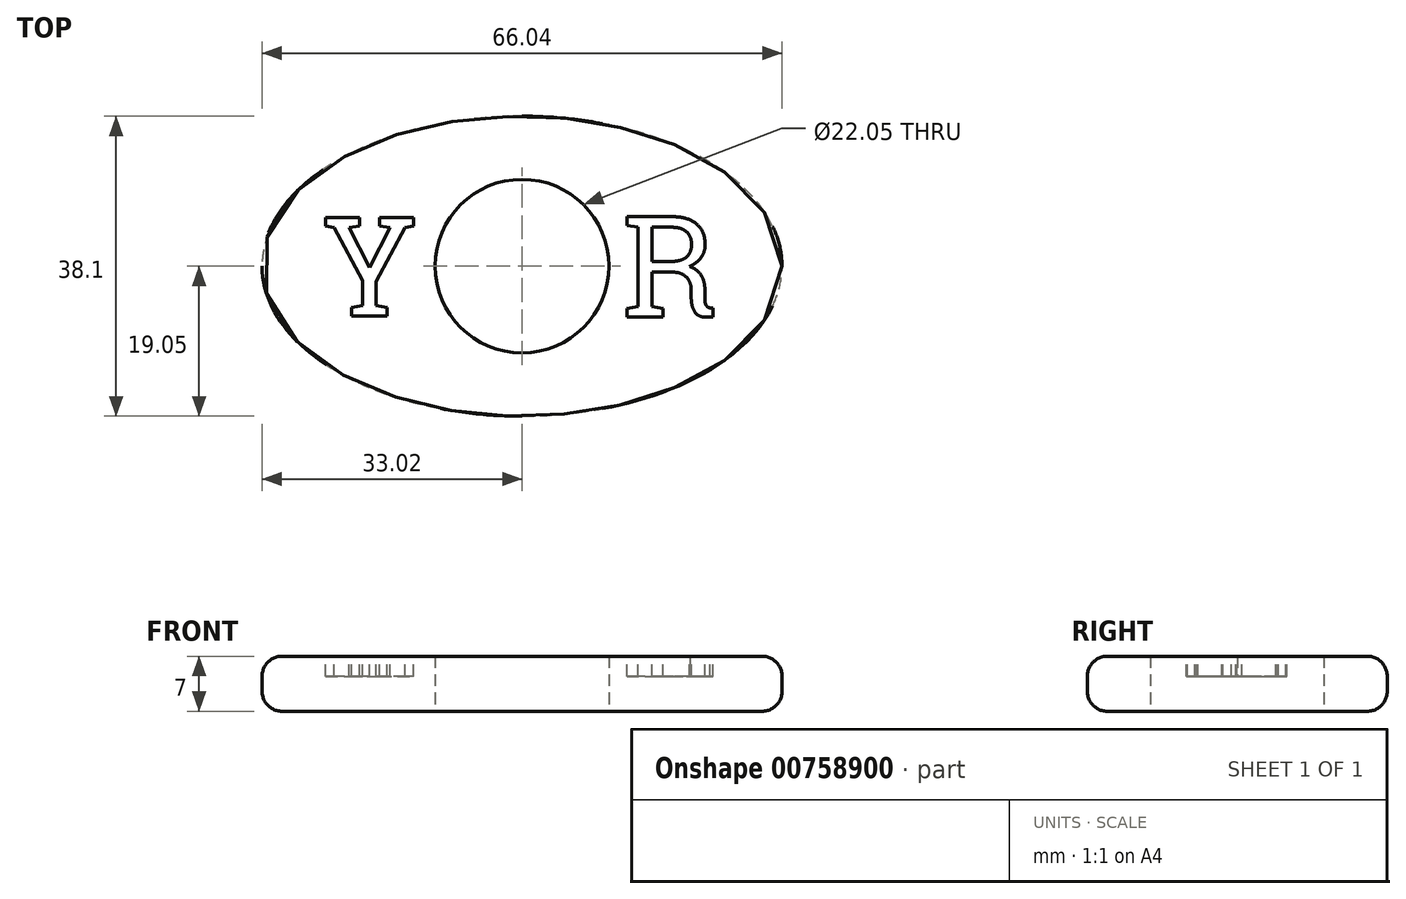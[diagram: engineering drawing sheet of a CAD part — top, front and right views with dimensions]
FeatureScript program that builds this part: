
annotation { "Feature Type Name" : "Feature", "Feature Type Description" : "" }
export const myFeature = defineFeature(function(context is Context, id is Id, definition is map)
    precondition{}
    {
        {
            var Q0;
            Q0=qCreatedBy(makeId("Top.planeOp"),FACE);
            var sketch = newSketch(context, id + "F0", { "sketchPlane" : qUnion([Q0])});
            skEllipse(sketch, "E0", {"center": v(0, 0) * mm, "majorRadius": 33.02 * mm, "minorRadius": 19.05 * mm, "majorAxis": v(1, 0)});
            skCircle(sketch, "E1", {"center": v(0, 0) * mm, "radius": 11.03 * mm});
            skLineSegment(sketch, "E2", {"start": v(-33.02, 0) * mm, "end": v(33.02, 0) * mm, "construction": true});
            skLineSegment(sketch, "E3", {"start": v(0, 19.05) * mm, "end": v(0, -19.05) * mm, "construction": true});
            skSolve(sketch);
        }
        {
            var Q0;
            Q0=makeQuery(id+"F0.imprint","IMPRINT",FACE,{"disambiguationData":[TD([[makeQuery(id+"F0.imprint","IMPRINT",EDGE,{"derivedFrom":sQuery(id+"F0.wireOp",EDGE,"E0")}),1.0]])]});
            extrude(context, id + "F1", {"entities" : qUnion([Q0]), "depth" : 7 * mm, "offsetDistance" : 25.4 * mm});
        }
        {
            var Q0;
            Q0=makeQuery(id+"F1.opExtrude","CAP_EDGE",EDGE,{"disambiguationData":[OSD([sQuery(id+"F0.wireOp",EDGE,"E0")])],"isStart":false});
            var Q1;
            Q1=makeQuery(id+"F1.opExtrude","CAP_EDGE",EDGE,{"disambiguationData":[OSD([sQuery(id+"F0.wireOp",EDGE,"E0")])],"isStart":true});
            fillet(context, id + "F2", {"entities" : qUnion([Q0, Q1]), "radius" : 2.54 * mm, "tangentPropagation" : true, "allowEdgeOverflow" : false});
        }
        {
            var Q0;
            Q0=makeQuery(id+"F1.opExtrude","CAP_FACE",FACE,{"disambiguationData":[OSD([sQuery(id+"F0.wireOp",EDGE,"E0"),sQuery(id+"F0.wireOp",EDGE,"E1")])],"isStart":false});
            var sketch = newSketch(context, id + "F3", { "sketchPlane" : qUnion([Q0])});
            skSolve(sketch);
        }
        {
            var Q0;
            {var subQ0=sQuery(id+"F0.wireOp",EDGE,"E1");Q0=makeQuery(id+"F3.imprint","IMPRINT",FACE,{"disambiguationData":[TD([[makeQuery(id+"F3.imprint","IMPRINT",EDGE,{"derivedFrom":makeQuery(id+"F1.opExtrude","CAP_EDGE",EDGE,{"disambiguationData":[OSD([subQ0])],"isStart":false})}),-1.0]])]});}
            var sketch = newSketch(context, id + "F4", { "sketchPlane" : qUnion([Q0])});
            skText(sketch, "E4", { "text": "Y", "fontName": "RobotoSlab-Regular.ttf"});
            skText(sketch, "E5", { "text": "R", "fontName": "RobotoSlab-Regular.ttf"});
            skLineSegment(sketch, "E6", {"start": v(0, 0) * mm, "end": v(-25.4, 0) * mm, "construction": true});
            skLineSegment(sketch, "E7", {"start": v(0, 0) * mm, "end": v(25.4, 0) * mm, "construction": true});
            skLineSegment(sketch, "E8", {"start": v(-25.4, 0) * mm, "end": v(-12.7, 0) * mm, "construction": true});
            skLineSegment(sketch, "E9", {"start": v(12.7, 0) * mm, "end": v(25.4, 0) * mm});
            skPoint(sketch, "E10", {"position": v(19.05, 0) * mm});
            skLineSegment(sketch, "E11", {"start": v(12.7, 0) * mm, "end": v(25.4, 0) * mm, "construction": true});
            skPoint(sketch, "E12", {"position": v(-19.05, 0) * mm});
            const initialGuessF4  = {"E4": [-0.0254, -0.00633, 1, 0, 0.01266], "E5": [0.0127, -0.00648, 1, 0, 0.01295]};
            skSetInitialGuess(sketch, initialGuessF4);
            skSolve(sketch);
        }
        {
            var Q0;
            Q0=qSketchRegion(id+"F4",true);
            extrude(context, id + "F5", {"entities" : qUnion([Q0]), "operationType" : NewBodyOperationType.REMOVE, "oppositeDirection" : true, "depth" : 2.54 * mm, "offsetDistance" : 25.4 * mm});
        }
    });
